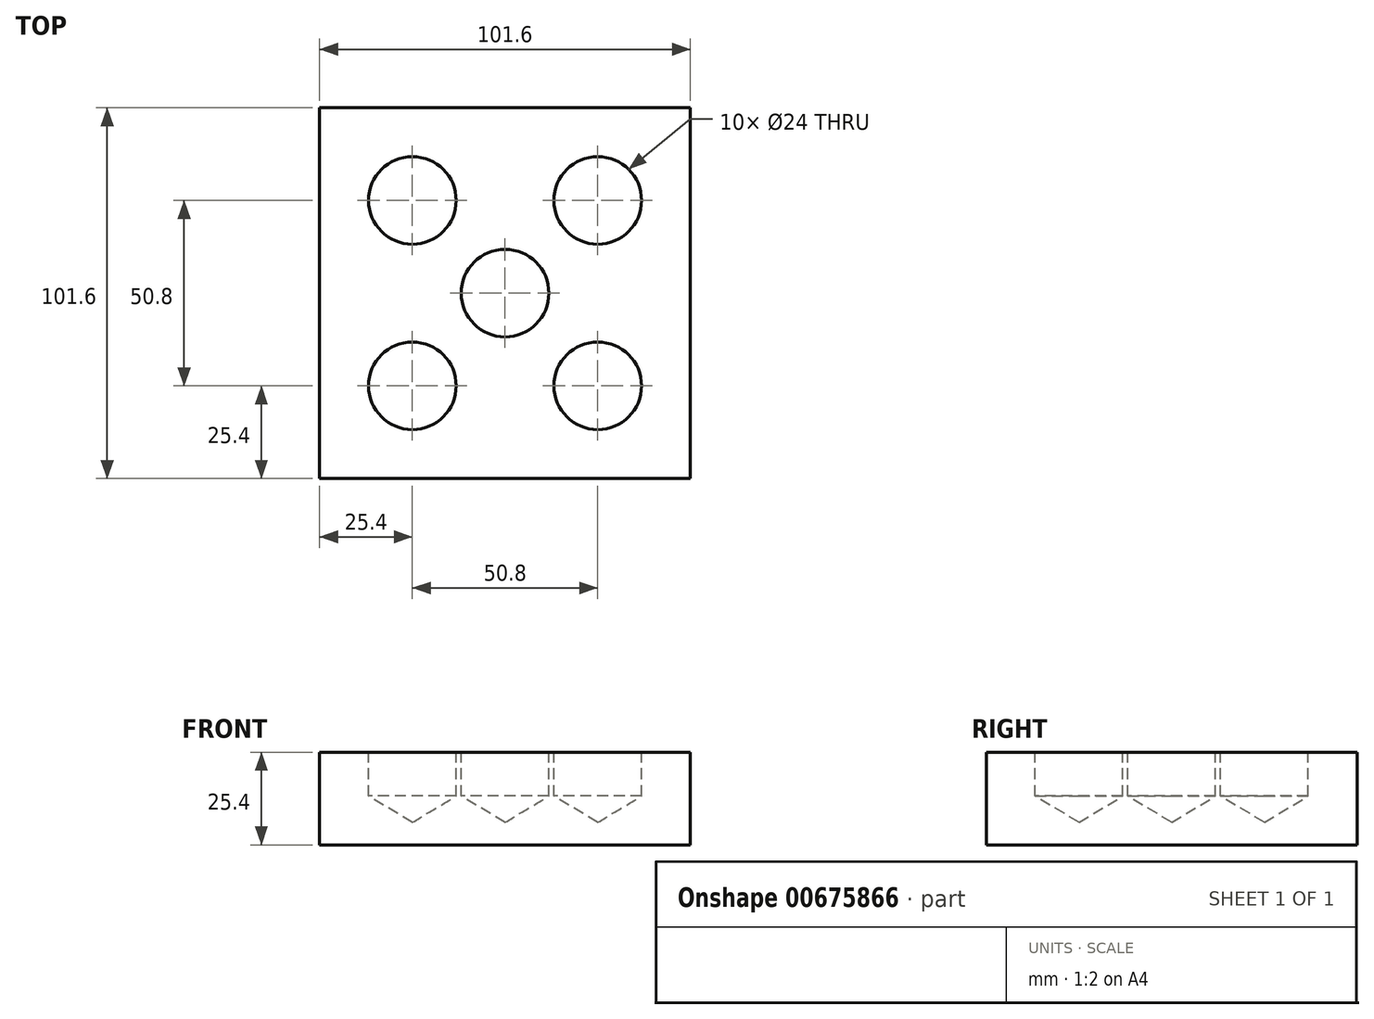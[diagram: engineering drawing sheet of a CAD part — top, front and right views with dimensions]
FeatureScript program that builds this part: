
annotation { "Feature Type Name" : "Feature", "Feature Type Description" : "" }
export const myFeature = defineFeature(function(context is Context, id is Id, definition is map)
    precondition{}
    {
        {
            var Q0;
            Q0=qCreatedBy(makeId("Top.planeOp"),FACE);
            var sketch = newSketch(context, id + "F0", { "sketchPlane" : qUnion([Q0])});
            skLineSegment(sketch, "E0.bottom", {"start": v(50.8, 50.8) * mm, "end": v(-50.8, 50.8) * mm});
            skLineSegment(sketch, "E0.top", {"start": v(50.8, -50.8) * mm, "end": v(-50.8, -50.8) * mm});
            skLineSegment(sketch, "E0.left", {"start": v(50.8, 50.8) * mm, "end": v(50.8, -50.8) * mm});
            skLineSegment(sketch, "E0.right", {"start": v(-50.8, 50.8) * mm, "end": v(-50.8, -50.8) * mm});
            skPoint(sketch, "E0.middle", {"position": v(0, 0) * mm});
            skSolve(sketch);
        }
        {
            var Q0;
            Q0 = qSketchRegion(id + "F0", true);
            extrude(context, id + "F1", {"entities" : qUnion([Q0]), "depth" : 25.4 * mm, "offsetDistance" : 25.4 * mm});
        }
        {
            var Q0;
            Q0=makeQuery(id+"F1.opExtrude","CAP_FACE",FACE,{"disambiguationData":[OSD([sQuery(id+"F0.wireOp",EDGE,"E0.bottom"),sQuery(id+"F0.wireOp",EDGE,"E0.top"),sQuery(id+"F0.wireOp",EDGE,"E0.left"),sQuery(id+"F0.wireOp",EDGE,"E0.right")])],"isStart":false});
            var sketch = newSketch(context, id + "F2", { "sketchPlane" : qUnion([Q0])});
            skPoint(sketch, "E1", {"position": v(0, 0) * mm});
            skPoint(sketch, "E2", {"position": v(-25.4, 25.4) * mm});
            skPoint(sketch, "E3", {"position": v(25.4, 25.4) * mm});
            skPoint(sketch, "E4", {"position": v(25.4, -25.4) * mm});
            skPoint(sketch, "E5", {"position": v(-25.4, -25.4) * mm});
            skSolve(sketch);
        }
        {
            var Q0;
            Q0=sQuery(id+"F2.wireOp",VERTEX,"E2");
            var Q1;
            Q1=sQuery(id+"F2.wireOp",VERTEX,"E3");
            var Q2;
            Q2=sQuery(id+"F2.wireOp",VERTEX,"E1");
            var Q3;
            Q3=sQuery(id+"F2.wireOp",VERTEX,"E4");
            var Q4;
            Q4=sQuery(id+"F2.wireOp",VERTEX,"E5");
            var Q5;
            Q5=makeQuery(id+"F1.opExtrude","SWEPT_BODY",BODY,{"disambiguationData":[OSD([sQuery(id+"F0.wireOp",EDGE,"E0.bottom"),sQuery(id+"F0.wireOp",EDGE,"E0.top"),sQuery(id+"F0.wireOp",EDGE,"E0.left"),sQuery(id+"F0.wireOp",EDGE,"E0.right")])]});
            hole(context, id + "F3", {"style" : HoleStyle.SIMPLE, "endStyle" : HoleEndStyle.BLIND, "holeDiameter" : 24 * mm, "majorDiameter" : 6.35 * mm, "holeDepth" : 12 * mm, "isTappedThrough" : true, "tappedDepth" : 12.7 * mm, "tapClearance" : 3, "locations" : qUnion([Q0, Q1, Q2, Q3, Q4]), "scope" : qUnion([Q5])});
        }
    });
